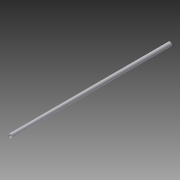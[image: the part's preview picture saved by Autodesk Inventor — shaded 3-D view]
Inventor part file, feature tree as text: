
AUTODESK INVENTOR PART (.ipt)
format: ipt  version: 2014 (Build 180170000, 170)  size: 70,144 bytes
history: native  units: in
note: dims shown in document units (in); Inventor stores cm internally (conversion verified against a paired STEP export)
features: extrude x1, sketch x1
ambient origin geometry x8: Origin, YZ Plane, XZ Plane, XY Plane, X Axis, Y Axis, Z Axis, Center Point
bodies: Solid1 (feature_tree)
feature tree (2):
  extrude  "Extrusion1"  Depth=96.5in
  sketch  "Sketch1"  dims[d0=2.375in d1=0.154in d2=96.5in d3=0.0in]
